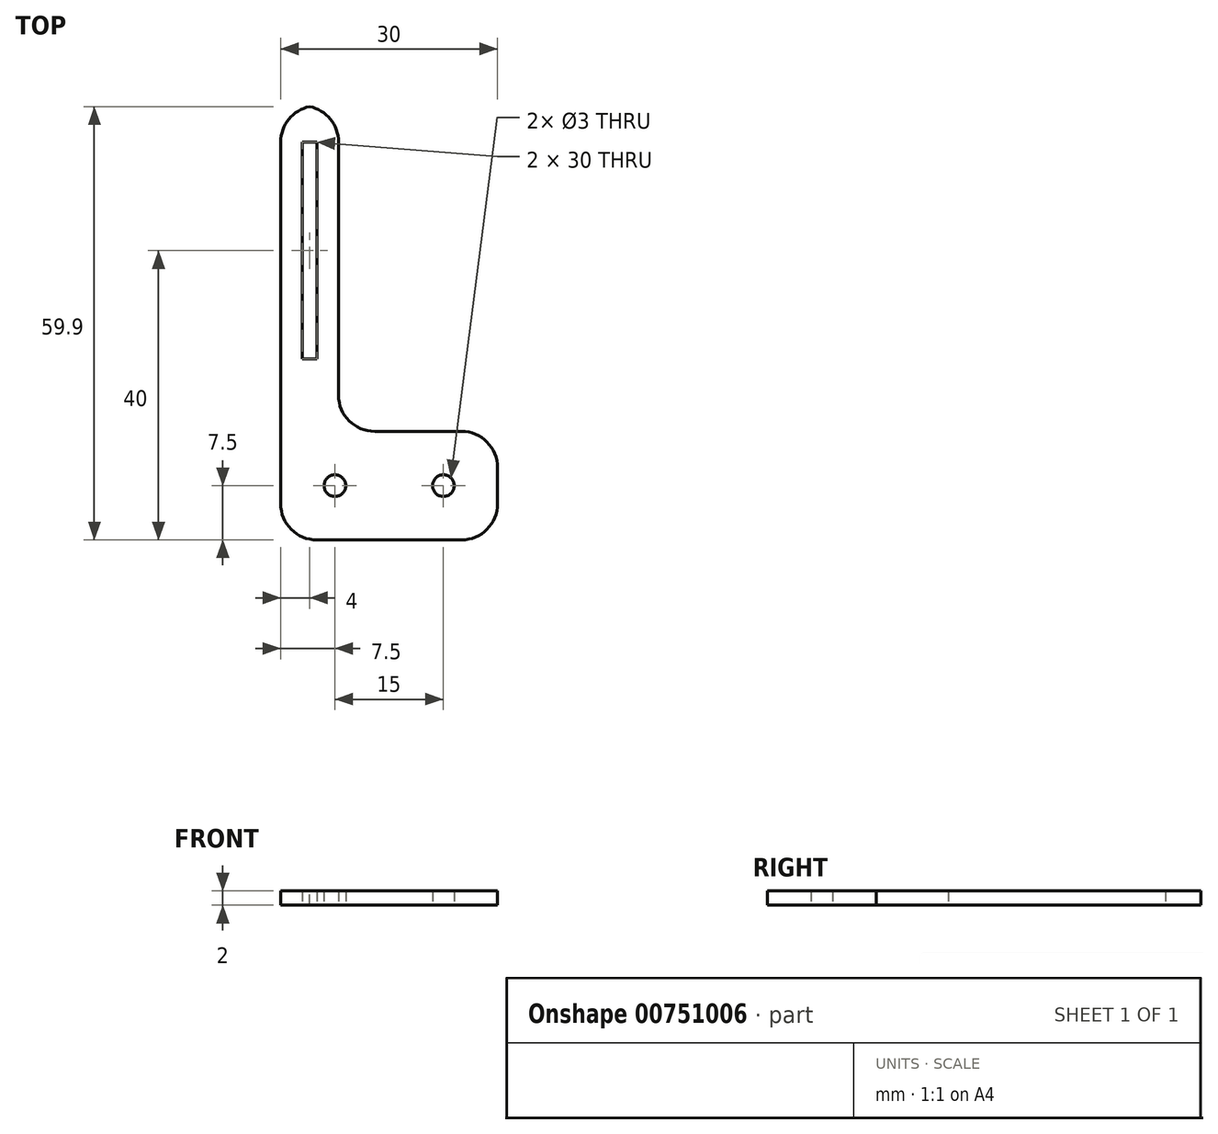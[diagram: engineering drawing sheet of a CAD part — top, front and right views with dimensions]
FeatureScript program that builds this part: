
annotation { "Feature Type Name" : "Feature", "Feature Type Description" : "" }
export const myFeature = defineFeature(function(context is Context, id is Id, definition is map)
    precondition{}
    {
        {
            var Q0;
            Q0=qCreatedBy(makeId("Top.planeOp"),FACE);
            var sketch = newSketch(context, id + "F0", { "sketchPlane" : qUnion([Q0])});
            skLineSegment(sketch, "E0.bottom", {"start": v(0, 0) * mm, "end": v(30, 0) * mm});
            skLineSegment(sketch, "E0.top", {"start": v(0, 15) * mm, "end": v(30, 15) * mm});
            skLineSegment(sketch, "E0.left", {"start": v(0, 0) * mm, "end": v(0, 15) * mm});
            skLineSegment(sketch, "E0.right", {"start": v(30, 0) * mm, "end": v(30, 15) * mm});
            skLineSegment(sketch, "E1.bottom", {"start": v(0, 15) * mm, "end": v(8, 15) * mm});
            skLineSegment(sketch, "E1.top", {"start": v(0, 60) * mm, "end": v(8, 60) * mm});
            skLineSegment(sketch, "E1.left", {"start": v(0, 15) * mm, "end": v(0, 60) * mm});
            skLineSegment(sketch, "E1.right", {"start": v(8, 15) * mm, "end": v(8, 60) * mm});
            skLineSegment(sketch, "E2", {"start": v(30, 7.5) * mm, "end": v(0, 7.5) * mm, "construction": true});
            skLineSegment(sketch, "E3.bottom", {"start": v(30, 5) * mm, "end": v(0, 5) * mm});
            skLineSegment(sketch, "E3.top", {"start": v(30, 10) * mm, "end": v(0, 10) * mm});
            skLineSegment(sketch, "E3.left", {"start": v(30, 5) * mm, "end": v(30, 10) * mm});
            skLineSegment(sketch, "E3.right", {"start": v(0, 5) * mm, "end": v(0, 10) * mm});
            skPoint(sketch, "E3.middle", {"position": v(15, 7.5) * mm});
            skLineSegment(sketch, "E4", {"start": v(4, 15) * mm, "end": v(4, 40) * mm});
            skLineSegment(sketch, "E5", {"start": v(15, 7.5) * mm, "end": v(30, 7.5) * mm});
            skLineSegment(sketch, "E6", {"start": v(15, 7.5) * mm, "end": v(0, 7.5) * mm});
            skPoint(sketch, "E7", {"position": v(7.5, 7.5) * mm});
            skPoint(sketch, "E8", {"position": v(22.5, 7.5) * mm});
            skCircle(sketch, "E9", {"center": v(22.5, 7.5) * mm, "radius": 1.5 * mm});
            skCircle(sketch, "E10", {"center": v(7.5, 7.5) * mm, "radius": 1.5 * mm});
            skLineSegment(sketch, "E11.bottom", {"start": v(5, 25) * mm, "end": v(3, 25) * mm});
            skLineSegment(sketch, "E11.top", {"start": v(5, 55) * mm, "end": v(3, 55) * mm});
            skLineSegment(sketch, "E11.left", {"start": v(5, 25) * mm, "end": v(5, 55) * mm});
            skLineSegment(sketch, "E11.right", {"start": v(3, 25) * mm, "end": v(3, 55) * mm});
            skPoint(sketch, "E11.middle", {"position": v(4, 40) * mm});
            skSolve(sketch);
        }
        {
            var Q0;
            {var subQ1=sQuery(id+"F0.wireOp",EDGE,"E0.top");Q0=makeQuery(id+"F0.imprint","IMPRINT",FACE,{"disambiguationData":[TD([[makeQuery(id+"F0.imprint","IMPRINT",EDGE,{"derivedFrom":subQ1}),-1.0]])]});}
            var Q1;
            {var subQ0=sQuery(id+"F0.wireOp",EDGE,"E0.bottom");Q1=makeQuery(id+"F0.imprint","IMPRINT",FACE,{"disambiguationData":[TD([[makeQuery(id+"F0.imprint","IMPRINT",EDGE,{"derivedFrom":subQ0}),1.0]])]});}
            var Q2;
            Q2=makeQuery(id+"F0.imprint","IMPRINT",FACE,{"disambiguationData":[TD([[makeQuery(id+"F0.imprint","IMPRINT",EDGE,{"derivedFrom":sQuery(id+"F0.wireOp",EDGE,"E3.bottom")}),-1.0]])]});
            var Q3;
            {var subQ1=sQuery(id+"F0.wireOp",EDGE,"E3.top");Q3=makeQuery(id+"F0.imprint","IMPRINT",FACE,{"disambiguationData":[TD([[makeQuery(id+"F0.imprint","IMPRINT",EDGE,{"derivedFrom":subQ1}),1.0]])]});}
            var Q4;
            {var subQ0=sQuery(id+"F0.wireOp",EDGE,"e8ad110d-cb6f-424f-91cf-8345e09232fa.0");var subQ1=sQuery(id+"F0.wireOp",EDGE,"E3.bottom");var subQ2=makeQuery(id+"F0.imprint","INTERSECT",VERTEX,{"disambiguationData":[OD(0.0)],"derivedFrom":[subQ1,subQ0]});Q4=makeQuery(id+"F0.imprint","IMPRINT",FACE,{"disambiguationData":[TD([[makeQuery(id+"F0.imprint","IMPRINT",EDGE,{"disambiguationData":[TD([[subQ2,-1.0]])],"derivedFrom":subQ1}),1.0]])]});}
            var Q5;
            {var subQ3=sQuery(id+"F0.wireOp",EDGE,"e8ad110d-cb6f-424f-91cf-8345e09232fa.0");var subQ5=sQuery(id+"F0.wireOp",EDGE,"E3.bottom");var subQ6=makeQuery(id+"F0.imprint","INTERSECT",VERTEX,{"disambiguationData":[OD(0.0)],"derivedFrom":[subQ5,subQ3]});Q5=makeQuery(id+"F0.imprint","IMPRINT",FACE,{"disambiguationData":[TD([[makeQuery(id+"F0.imprint","IMPRINT",EDGE,{"disambiguationData":[TD([[subQ6,-1.0]])],"derivedFrom":subQ5}),-1.0]])]});}
            var Q6;
            {var subQ3=sQuery(id+"F0.wireOp",EDGE,"e8ad110d-cb6f-424f-91cf-8345e09232fa.0");var subQ5=sQuery(id+"F0.wireOp",EDGE,"E3.top");var subQ6=makeQuery(id+"F0.imprint","INTERSECT",VERTEX,{"disambiguationData":[OD(0.0)],"derivedFrom":[subQ5,subQ3]});Q6=makeQuery(id+"F0.imprint","IMPRINT",FACE,{"disambiguationData":[TD([[makeQuery(id+"F0.imprint","IMPRINT",EDGE,{"disambiguationData":[TD([[subQ6,-1.0]])],"derivedFrom":subQ5}),1.0]])]});}
            var Q7;
            {var subQ0=sQuery(id+"F0.wireOp",EDGE,"e8ad110d-cb6f-424f-91cf-8345e09232fa.0");var subQ1=sQuery(id+"F0.wireOp",EDGE,"E3.top");var subQ2=makeQuery(id+"F0.imprint","INTERSECT",VERTEX,{"disambiguationData":[OD(0.0)],"derivedFrom":[subQ1,subQ0]});Q7=makeQuery(id+"F0.imprint","IMPRINT",FACE,{"disambiguationData":[TD([[makeQuery(id+"F0.imprint","IMPRINT",EDGE,{"disambiguationData":[TD([[subQ2,-1.0]])],"derivedFrom":subQ1}),-1.0]])]});}
            var Q8;
            {var subQ0=sQuery(id+"F0.wireOp",EDGE,"ea01a3ea-ce51-4154-88a3-5c0cfb0ecabd.0");var subQ1=sQuery(id+"F0.wireOp",EDGE,"E3.top");var subQ2=makeQuery(id+"F0.imprint","INTERSECT",VERTEX,{"disambiguationData":[OD(0.0)],"derivedFrom":[subQ1,subQ0]});Q8=makeQuery(id+"F0.imprint","IMPRINT",FACE,{"disambiguationData":[TD([[makeQuery(id+"F0.imprint","IMPRINT",EDGE,{"disambiguationData":[TD([[subQ2,-1.0]])],"derivedFrom":subQ1}),-1.0]])]});}
            var Q9;
            {var subQ3=sQuery(id+"F0.wireOp",EDGE,"ea01a3ea-ce51-4154-88a3-5c0cfb0ecabd.0");var subQ7=sQuery(id+"F0.wireOp",EDGE,"E3.top");var subQ8=makeQuery(id+"F0.imprint","INTERSECT",VERTEX,{"disambiguationData":[OD(0.0)],"derivedFrom":[subQ7,subQ3]});Q9=makeQuery(id+"F0.imprint","IMPRINT",FACE,{"disambiguationData":[TD([[makeQuery(id+"F0.imprint","IMPRINT",EDGE,{"disambiguationData":[TD([[subQ8,-1.0]])],"derivedFrom":subQ7}),1.0]])]});}
            var Q10;
            {var subQ4=sQuery(id+"F0.wireOp",EDGE,"ea01a3ea-ce51-4154-88a3-5c0cfb0ecabd.0");var subQ7=sQuery(id+"F0.wireOp",EDGE,"E3.bottom");var subQ8=makeQuery(id+"F0.imprint","INTERSECT",VERTEX,{"disambiguationData":[OD(0.0)],"derivedFrom":[subQ7,subQ4]});Q10=makeQuery(id+"F0.imprint","IMPRINT",FACE,{"disambiguationData":[TD([[makeQuery(id+"F0.imprint","IMPRINT",EDGE,{"disambiguationData":[TD([[subQ8,-1.0]])],"derivedFrom":subQ7}),-1.0]])]});}
            var Q11;
            {var subQ0=sQuery(id+"F0.wireOp",EDGE,"ea01a3ea-ce51-4154-88a3-5c0cfb0ecabd.0");var subQ1=sQuery(id+"F0.wireOp",EDGE,"E3.bottom");var subQ2=makeQuery(id+"F0.imprint","INTERSECT",VERTEX,{"disambiguationData":[OD(0.0)],"derivedFrom":[subQ1,subQ0]});Q11=makeQuery(id+"F0.imprint","IMPRINT",FACE,{"disambiguationData":[TD([[makeQuery(id+"F0.imprint","IMPRINT",EDGE,{"disambiguationData":[TD([[subQ2,-1.0]])],"derivedFrom":subQ1}),1.0]])]});}
            var Q12;
            {var subQ0=sQuery(id+"F0.wireOp",EDGE,"e8ad110d-cb6f-424f-91cf-8345e09232fa.0");var subQ1=sQuery(id+"F0.wireOp",EDGE,"E3.bottom");var subQ2=makeQuery(id+"F0.imprint","INTERSECT",VERTEX,{"disambiguationData":[OD(1.0)],"derivedFrom":[subQ1,subQ0]});Q12=makeQuery(id+"F0.imprint","IMPRINT",FACE,{"disambiguationData":[TD([[makeQuery(id+"F0.imprint","IMPRINT",EDGE,{"disambiguationData":[TD([[subQ2,-1.0]])],"derivedFrom":subQ1}),-1.0]])]});}
            var Q13;
            {var subQ5=sQuery(id+"F0.wireOp",EDGE,"e8ad110d-cb6f-424f-91cf-8345e09232fa.0");var subQ6=sQuery(id+"F0.wireOp",EDGE,"E3.top");var subQ7=makeQuery(id+"F0.imprint","INTERSECT",VERTEX,{"disambiguationData":[OD(1.0)],"derivedFrom":[subQ6,subQ5]});Q13=makeQuery(id+"F0.imprint","IMPRINT",FACE,{"disambiguationData":[TD([[makeQuery(id+"F0.imprint","IMPRINT",EDGE,{"disambiguationData":[TD([[subQ7,-1.0]])],"derivedFrom":subQ6}),1.0]])]});}
            var Q14;
            {var subQ0=sQuery(id+"F0.wireOp",EDGE,"e8ad110d-cb6f-424f-91cf-8345e09232fa.0");var subQ3=sQuery(id+"F0.wireOp",EDGE,"E3.top");var subQ4=makeQuery(id+"F0.imprint","INTERSECT",VERTEX,{"disambiguationData":[OD(1.0)],"derivedFrom":[subQ3,subQ0]});Q14=makeQuery(id+"F0.imprint","IMPRINT",FACE,{"disambiguationData":[TD([[makeQuery(id+"F0.imprint","IMPRINT",EDGE,{"disambiguationData":[TD([[subQ4,-1.0]])],"derivedFrom":subQ3}),-1.0]])]});}
            var Q15;
            {var subQ0=sQuery(id+"F0.wireOp",EDGE,"E1.bottom");var subQ5=sQuery(id+"F0.wireOp",EDGE,"ea01a3ea-ce51-4154-88a3-5c0cfb0ecabd.0");var subQ6=makeQuery(id+"F0.imprint","INTERSECT",VERTEX,{"disambiguationData":[OD(0.0)],"derivedFrom":[subQ0,subQ5]});Q15=makeQuery(id+"F0.imprint","IMPRINT",FACE,{"disambiguationData":[TD([[makeQuery(id+"F0.imprint","IMPRINT",EDGE,{"disambiguationData":[TD([[subQ6,-1.0]])],"derivedFrom":subQ5}),-1.0]])]});}
            var Q16;
            {var subQ0=sQuery(id+"F0.wireOp",EDGE,"E4");var subQ1=sQuery(id+"F0.wireOp",EDGE,"E1.bottom");var subQ2=makeQuery(id+"F0.imprint","INTERSECT",VERTEX,{"derivedFrom":[subQ1,subQ0]});Q16=makeQuery(id+"F0.imprint","IMPRINT",FACE,{"disambiguationData":[TD([[makeQuery(id+"F0.imprint","IMPRINT",EDGE,{"disambiguationData":[TD([[subQ2,1.0]])],"derivedFrom":subQ1}),1.0]])]});}
            var Q17;
            Q17=makeQuery(id+"F0.imprint","IMPRINT",FACE,{"disambiguationData":[TD([[makeQuery(id+"F0.imprint","IMPRINT",EDGE,{"derivedFrom":sQuery(id+"F0.wireOp",EDGE,"E1.top")}),-1.0]])]});
            var Q18;
            {var subQ0=sQuery(id+"F0.wireOp",EDGE,"E4");var subQ1=sQuery(id+"F0.wireOp",EDGE,"E1.bottom");var subQ2=makeQuery(id+"F0.imprint","INTERSECT",VERTEX,{"derivedFrom":[subQ1,subQ0]});Q18=makeQuery(id+"F0.imprint","IMPRINT",FACE,{"disambiguationData":[TD([[makeQuery(id+"F0.imprint","IMPRINT",EDGE,{"disambiguationData":[TD([[subQ2,-1.0]])],"derivedFrom":subQ1}),1.0]])]});}
            extrude(context, id + "F1", {"entities" : qUnion([Q0, Q1, Q2, Q3, Q4, Q5, Q6, Q7, Q8, Q9, Q10, Q11, Q12, Q13, Q14, Q15, Q16, Q17, Q18]), "depth" : 2 * mm, "offsetDistance" : 25 * mm});
        }
        {
            var Q0;
            Q0=makeQuery(id+"F1.opExtrude","SWEPT_EDGE",EDGE,{"disambiguationData":[OSD([sQuery(id+"F0.wireOp",EDGE,"E0.top"),sQuery(id+"F0.wireOp",EDGE,"E1.bottom"),sQuery(id+"F0.wireOp",EDGE,"E1.right")])]});
            var Q1;
            Q1=makeQuery(id+"F1.opExtrude","SWEPT_EDGE",EDGE,{"disambiguationData":[OSD([sQuery(id+"F0.wireOp",EDGE,"E0.top"),sQuery(id+"F0.wireOp",EDGE,"E0.right")])]});
            var Q2;
            Q2=makeQuery(id+"F1.opExtrude","SWEPT_EDGE",EDGE,{"disambiguationData":[OSD([sQuery(id+"F0.wireOp",EDGE,"E0.bottom"),sQuery(id+"F0.wireOp",EDGE,"E0.right")])]});
            var Q3;
            Q3=makeQuery(id+"F1.opExtrude","SWEPT_EDGE",EDGE,{"disambiguationData":[OSD([sQuery(id+"F0.wireOp",EDGE,"E0.bottom"),sQuery(id+"F0.wireOp",EDGE,"E0.left")])]});
            fillet(context, id + "F2", {"entities" : qUnion([Q0, Q1, Q2, Q3]), "radius" : 5 * mm, "tangentPropagation" : true, "allowEdgeOverflow" : false});
        }
        {
            var Q0;
            Q0=makeQuery(id+"F1.opExtrude","SWEPT_EDGE",EDGE,{"disambiguationData":[OSD([sQuery(id+"F0.wireOp",EDGE,"E1.top"),sQuery(id+"F0.wireOp",EDGE,"E1.right")])]});
            var Q1;
            Q1=makeQuery(id+"F1.opExtrude","SWEPT_EDGE",EDGE,{"disambiguationData":[OSD([sQuery(id+"F0.wireOp",EDGE,"E1.top"),sQuery(id+"F0.wireOp",EDGE,"E1.left")])]});
            fillet(context, id + "F3", {"entities" : qUnion([Q0, Q1]), "radius" : 5 * mm, "tangentPropagation" : true, "allowEdgeOverflow" : false});
        }
    });
